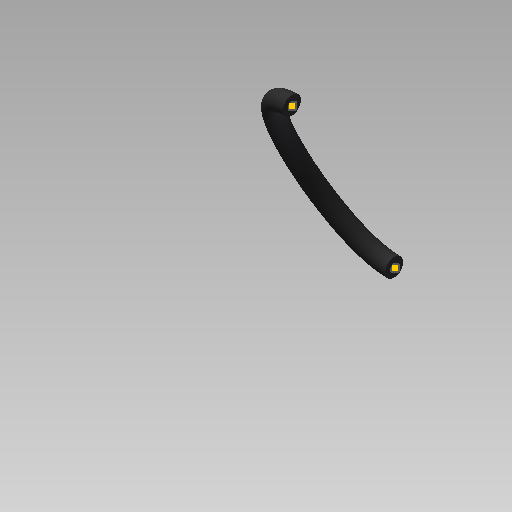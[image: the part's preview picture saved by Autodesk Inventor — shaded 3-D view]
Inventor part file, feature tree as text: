
AUTODESK INVENTOR PART (.ipt)
format: ipt  version: 2019 (Build 230136000, 136)  size: 309,760 bytes
history: native  units: mm (DEFAULTED — no unit token found)
features: other x3, sketch x2, plane x1, sweep x1
ambient origin geometry x8: Origin, YZ Plane, XZ Plane, XY Plane, X Axis, Y Axis, Z Axis, Center Point
bodies: Body1 (feature_tree)
feature tree (7):
  sketch  "Boceto 3D1"  dims[d4=-10.0mm d5=10.0mm]
  other  "Punto de trabajo3"
  other  "Punto de trabajo4"
  plane  "Plano de trabajo1"
  sketch  "Boceto2"  dims[d6=0.0mm d7=0.0mm]
  other  "Punto de trabajo5"
  sweep  "Barrido1"
